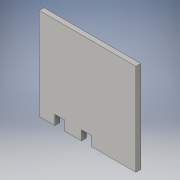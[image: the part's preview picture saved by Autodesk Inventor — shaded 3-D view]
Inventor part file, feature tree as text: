
AUTODESK INVENTOR PART (.ipt)
format: ipt  version: 2016 (Build 200138000, 138)  size: 112,640 bytes
history: native  units: in
note: dims shown in document units (in); Inventor stores cm internally (conversion verified against a paired STEP export)
features: extrude x2, sketch x2
ambient origin geometry x8: Origin, YZ Plane, XZ Plane, XY Plane, X Axis, Y Axis, Z Axis, Center Point
bodies: Solid1 (feature_tree)
feature tree (4):
  extrude  "Extrusion1"  Depth=9.5in
  extrude  "Extrusion2"  Depth=0.5in
  sketch  "Sketch1"  dims[d0=10.0in d1=9.5in]
  sketch  "Sketch2"  dims[d2=0.5in d3=0.0in d4=3.5in d5=0.875in d6=0.875in d7=1.0in d8=1.0in d9=1.0in d10=0.875in d11=0.875in d12=0.5in d13=0.0in]
